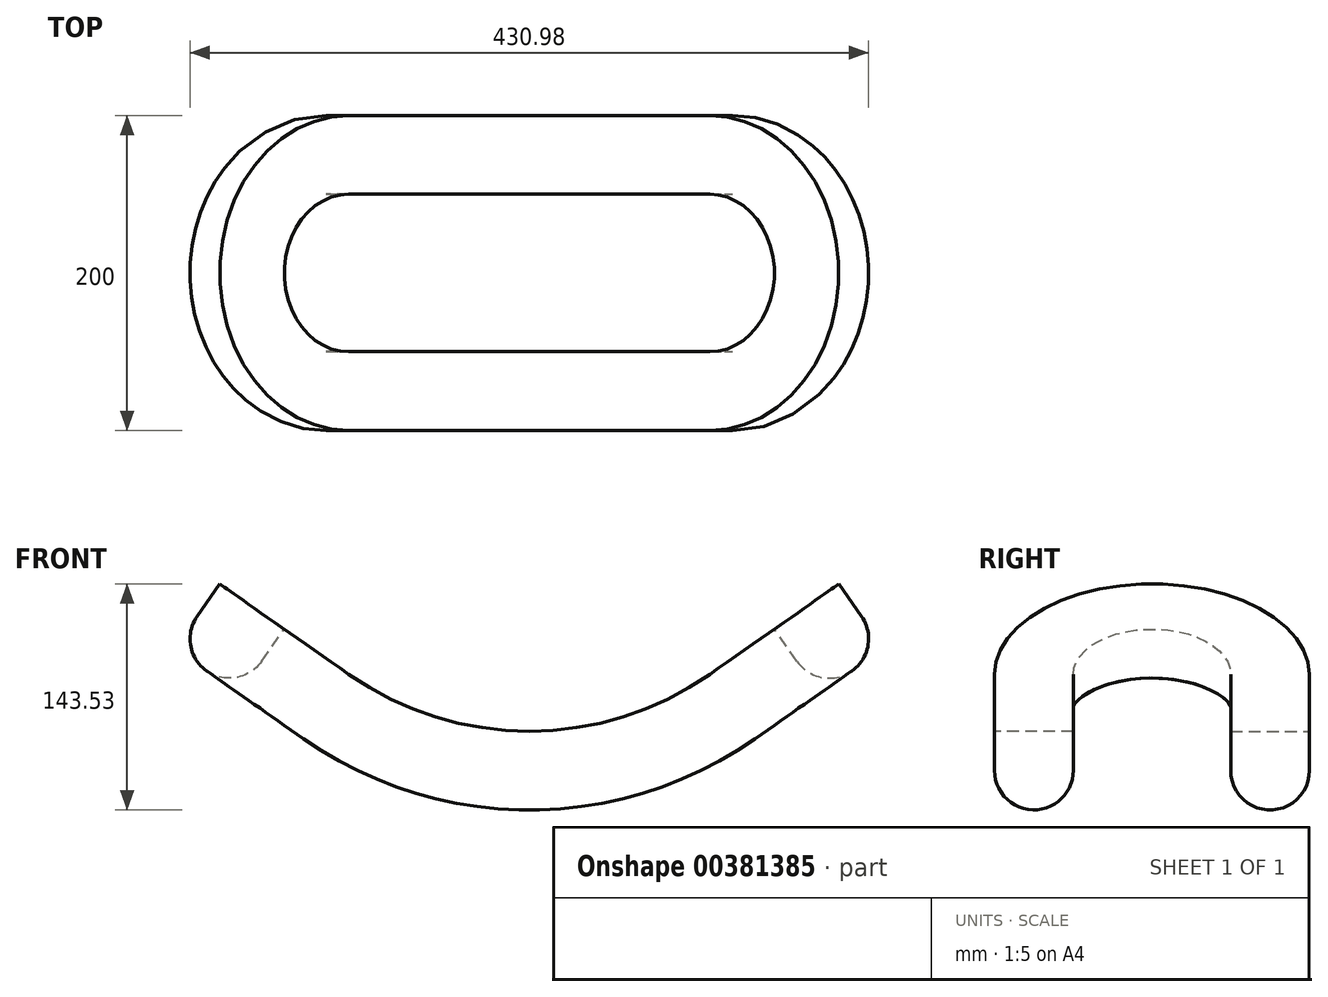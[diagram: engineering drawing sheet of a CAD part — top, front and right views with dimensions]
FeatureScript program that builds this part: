
annotation { "Feature Type Name" : "Feature", "Feature Type Description" : "" }
export const myFeature = defineFeature(function(context is Context, id is Id, definition is map)
    precondition{}
    {
        {
            var Q0;
            Q0=qCreatedBy(makeId("Front.planeOp"),FACE);
            var sketch = newSketch(context, id + "F0", { "sketchPlane" : qUnion([Q0])});
            skArc(sketch, "E0", {"start": v(0, 0) * mm, "mid": v(60.14, 9.26) * mm, "end": v(114.72, 36.17) * mm});
            skLineSegment(sketch, "E1", {"start": v(114.72, 36.17) * mm, "end": v(196.63, 93.53) * mm});
            skLineSegment(sketch, "E2", {"start": v(0, 200) * mm, "end": v(114.72, 36.17) * mm, "construction": true});
            skSolve(sketch);
        }
        {
            var Q0;
            Q0=sQuery(id+"F0.wireOp",EDGE,"E0");
            var Q1;
            Q1=sQuery(id+"F0.wireOp",EDGE,"E1");
            extrude(context, id + "F1", {"bodyType" : ToolBodyType.SURFACE, "surfaceEntities" : qUnion([Q0, Q1]), "depth" : 100 * mm});
        }
        {
            var Q0;
            Q0=makeQuery(id+"F1.opExtrude","SWEPT_FACE",FACE,{"disambiguationData":[OSD([sQuery(id+"F0.wireOp",EDGE,"E1")])]});
            var sketch = newSketch(context, id + "F2", { "sketchPlane" : qUnion([Q0])});
            skArc(sketch, "E3", {"start": v(114.72, 100) * mm, "mid": v(185.43, 70.71) * mm, "end": v(214.72, 0) * mm});
            skSolve(sketch);
        }
        {
            var Q0;
            Q0=qCreatedBy(makeId("Right.planeOp"),FACE);
            var sketch = newSketch(context, id + "F3", { "sketchPlane" : qUnion([Q0])});
            skLineSegment(sketch, "E4", {"start": v(-100, 0) * mm, "end": v(-100, -25) * mm});
            skLineSegment(sketch, "E5", {"start": v(-100, 0) * mm, "end": v(-50, 0) * mm});
            skLineSegment(sketch, "E6", {"start": v(-50, 0) * mm, "end": v(-50, -25) * mm});
            skLineSegment(sketch, "E7", {"start": v(-50, -25) * mm, "end": v(-100, -25) * mm, "construction": true});
            skArc(sketch, "E8", {"start": v(-50, -25) * mm, "mid": v(-75, -50) * mm, "end": v(-100, -25) * mm});
            skSolve(sketch);
        }
        {
            var Q0;
            Q0=makeQuery(id+"F3.imprint","IMPRINT",FACE,{"disambiguationData":[TD([[makeQuery(id+"F3.imprint","IMPRINT",EDGE,{"derivedFrom":sQuery(id+"F3.wireOp",EDGE,"E4")}),1.0]])]});
            var Q1;
            Q1=makeQuery(id+"F1.opExtrude","CAP_EDGE",EDGE,{"disambiguationData":[OSD([sQuery(id+"F0.wireOp",EDGE,"E0")])],"isStart":false});
            var Q2;
            Q2=sQuery(id+"F2.wireOp",EDGE,"E3");
            sweep(context, id + "F4", {"profiles" : qUnion([Q0]), "path" : qUnion([Q1, Q2])});
        }
        {
            var Q0;
            Q0=makeQuery(id+"F4.opSweep","SWEPT_BODY",BODY,{"disambiguationData":[OSD([sQuery(id+"F2.wireOp",EDGE,"E3"),sQuery(id+"F3.wireOp",EDGE,"E4"),sQuery(id+"F3.wireOp",EDGE,"E5"),sQuery(id+"F3.wireOp",EDGE,"E6"),sQuery(id+"F3.wireOp",EDGE,"E8")])]});
            var Q1;
            Q1=qCreatedBy(makeId("Front.planeOp"),FACE);
            mirror(context, id + "F5", {"operationType" : NewBodyOperationType.ADD, "entities" : qUnion([Q0]), "mirrorPlane" : qUnion([Q1])});
        }
        {
            var Q0;
            Q0=makeQuery(id+"F4.opSweep","SWEPT_BODY",BODY,{"disambiguationData":[OSD([sQuery(id+"F2.wireOp",EDGE,"E3"),sQuery(id+"F3.wireOp",EDGE,"E4"),sQuery(id+"F3.wireOp",EDGE,"E5"),sQuery(id+"F3.wireOp",EDGE,"E6"),sQuery(id+"F3.wireOp",EDGE,"E8")])]});
            var Q1;
            Q1=qCreatedBy(makeId("Right.planeOp"),FACE);
            mirror(context, id + "F6", {"operationType" : NewBodyOperationType.ADD, "entities" : qUnion([Q0]), "mirrorPlane" : qUnion([Q1])});
        }
    });
